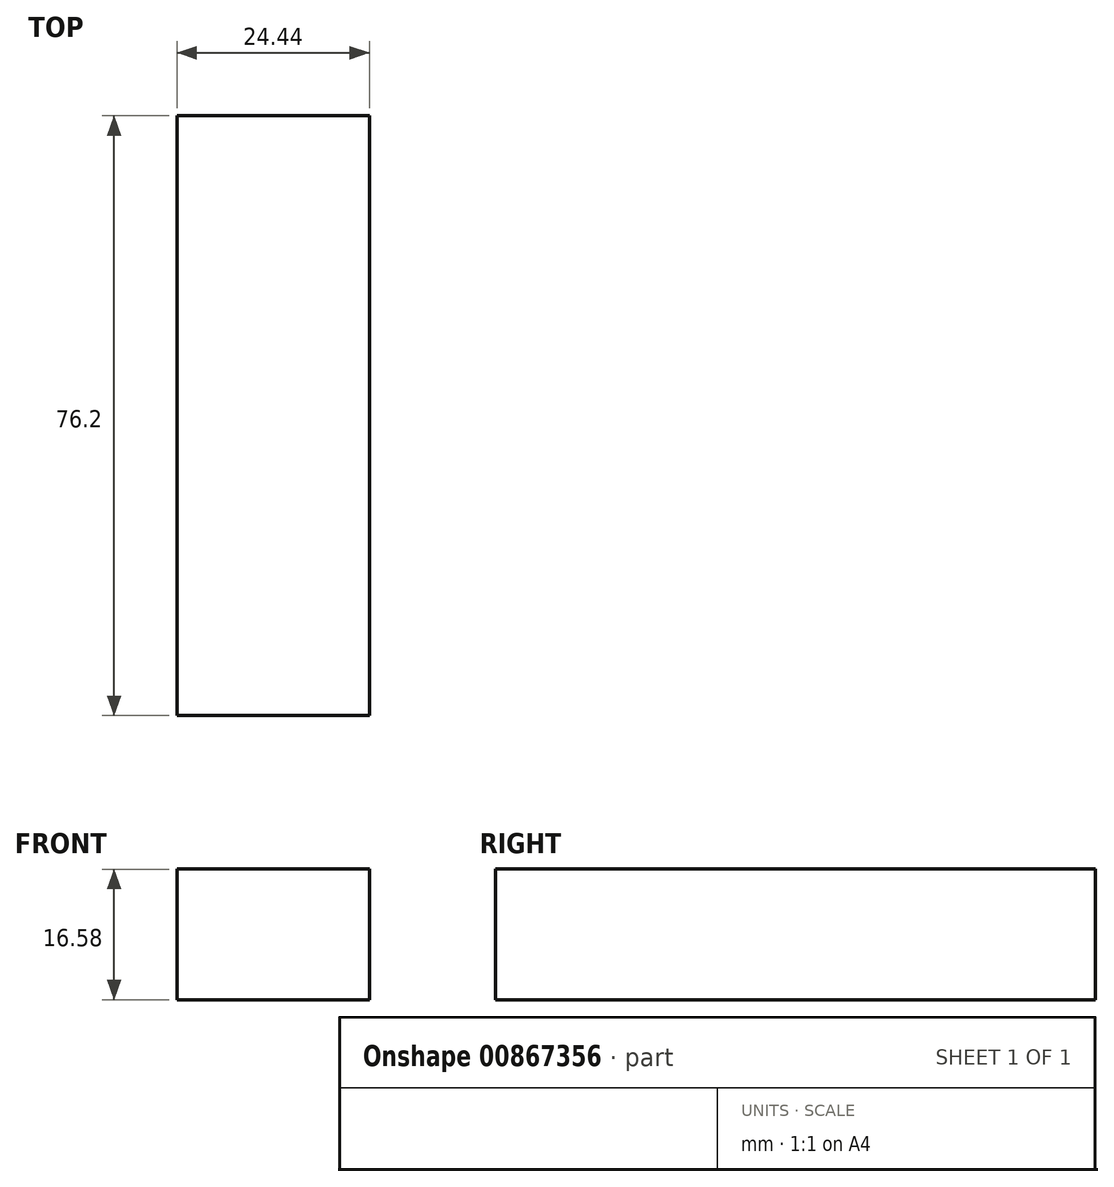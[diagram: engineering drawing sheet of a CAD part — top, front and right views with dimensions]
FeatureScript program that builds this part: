
annotation { "Feature Type Name" : "Feature", "Feature Type Description" : "" }
export const myFeature = defineFeature(function(context is Context, id is Id, definition is map)
    precondition{}
    {
        {
            var Q0;
            Q0=qCreatedBy(makeId("Front.planeOp"),FACE);
            var sketch = newSketch(context, id + "F0", { "sketchPlane" : qUnion([Q0])});
            skLineSegment(sketch, "E0.bottom", {"start": v(12.22, 8.3) * mm, "end": v(-12.22, 8.3) * mm});
            skLineSegment(sketch, "E0.top", {"start": v(12.22, -8.3) * mm, "end": v(-12.22, -8.3) * mm});
            skLineSegment(sketch, "E0.left", {"start": v(12.22, 8.3) * mm, "end": v(12.22, -8.3) * mm});
            skLineSegment(sketch, "E0.right", {"start": v(-12.22, 8.3) * mm, "end": v(-12.22, -8.3) * mm});
            skPoint(sketch, "E0.middle", {"position": v(0, 0) * mm});
            skSolve(sketch);
        }
        {
            var Q0;
            Q0 = qSketchRegion(id + "F0", true);
            extrude(context, id + "F1", {"entities" : qUnion([Q0]), "depth" : 76.2 * mm, "offsetDistance" : 25.4 * mm});
        }
    });
